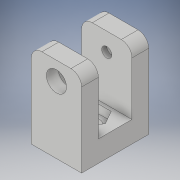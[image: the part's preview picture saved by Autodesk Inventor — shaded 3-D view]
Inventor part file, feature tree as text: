
AUTODESK INVENTOR PART (.ipt)
format: ipt  version: 2019 (Build 230136000, 136)  size: 193,536 bytes
history: native  units: in
note: dims shown in document units (in); Inventor stores cm internally (conversion verified against a paired STEP export)
features: extrude x9, sketch x9, projected_geometry x2, fillet x1
ambient origin geometry x8: Origin, YZ Plane, XZ Plane, XY Plane, X Axis, Y Axis, Z Axis, Center Point
bodies: Solid1 (feature_tree)
feature tree (21):
  extrude  "Extrusion1"  Depth=0.5906in
  extrude  "Extrusion2"  Depth=0.3937in
  extrude  "Extrusion3"  Depth=0.1181in
  fillet  "Fillet1"  Radius=0.75in
  extrude  "Extrusion4"  Depth=0.125in
  extrude  "Extrusion5"  Depth=0.315in
  extrude  "Extrusion6"  Depth=0.2362in
  extrude  "Extrusion7"  Depth=0.2205in
  extrude  "Extrusion8"  Depth=0.0394in TaperAngle=0.0deg
  extrude  "Extrusion9"  [1 undecoded]
  sketch  "Sketch1"  dims[d0=0.7087in d1=0.5906in]
  sketch  "Sketch2"  dims[d2=1.0in d3=0.0in d5=0.3937in]
  sketch  "Sketch3"  dims[d6=0.75in d7=0.0in d8=0.1181in d9=0.75in d10=0.0in]
  sketch  "Sketch4"  dims[d11=0.125in d12=0.2165in]
  sketch  "Sketch5"  dims[d13=0.75in d14=0.0in d15=0.315in]
  sketch  "Sketch6"  dims[d16=0.1in d17=0.0in d18=0.2362in]
  sketch  "Sketch7"  dims[d19=0.0984in d20=0.0in d21=0.2205in]
  sketch  "Sketch8"  dims[d22=0.0984in d23=0.0in d24=0.0394in d25=0.0in]
  projected_geometry  "Projected Loop1"
  sketch  "Sketch9"  dims[d26=0.0394in d27=0.0in]
  projected_geometry  "Projected Loop2"
note: 1 required parameter value undecoded (feature->parameter linkage not recoverable at this tier; creation-order binding heuristic only, values carry confidence <= 0.55)
